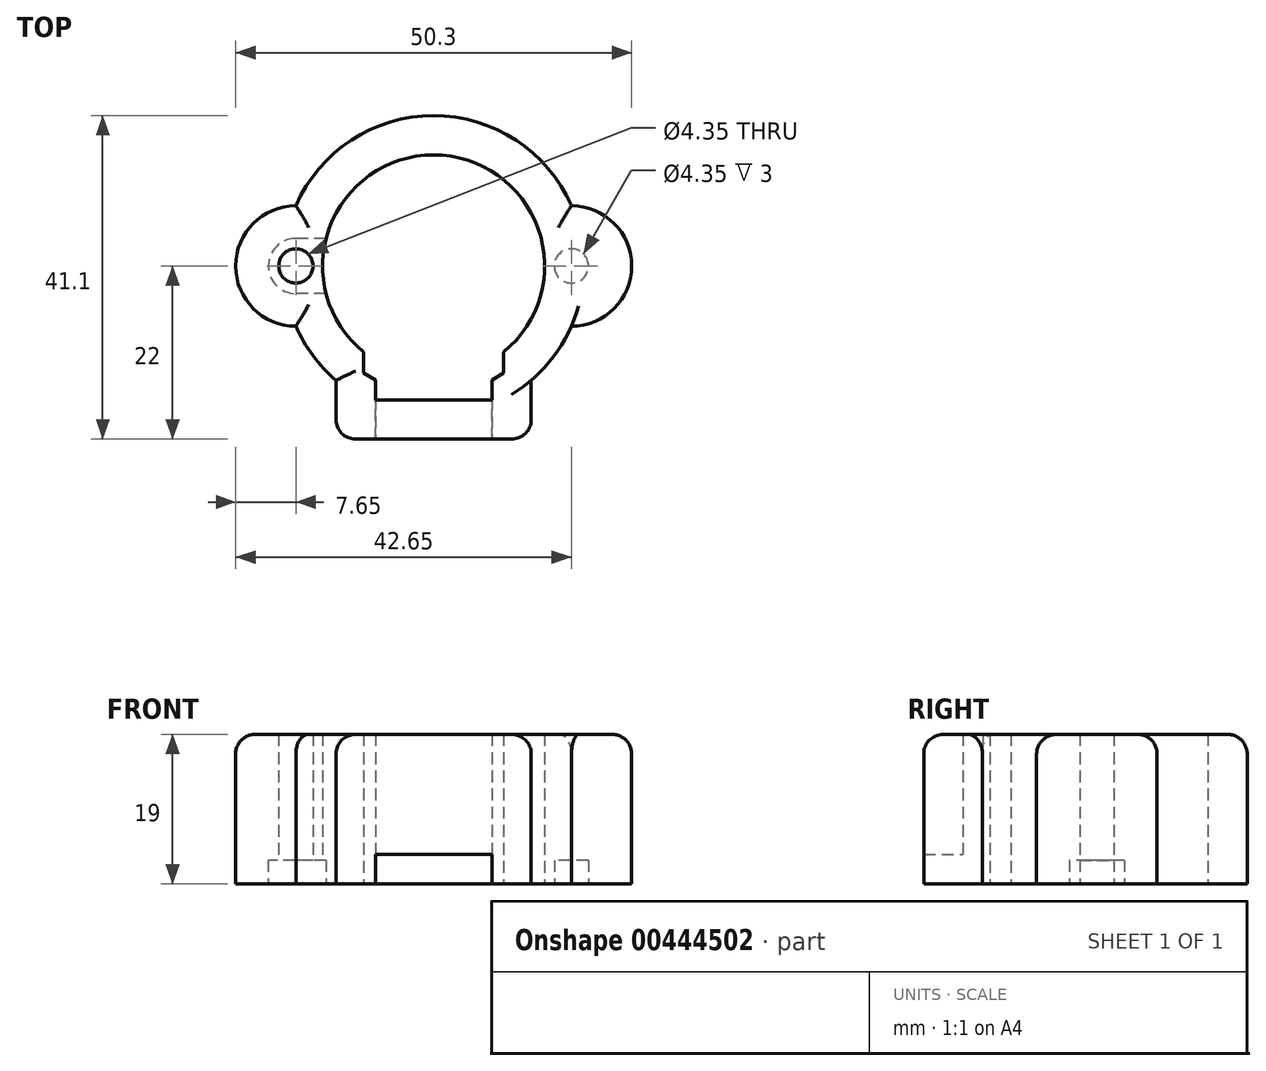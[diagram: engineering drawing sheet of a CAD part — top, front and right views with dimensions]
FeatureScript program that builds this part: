
annotation { "Feature Type Name" : "Feature", "Feature Type Description" : "" }
export const myFeature = defineFeature(function(context is Context, id is Id, definition is map)
    precondition{}
    {
        {
            var Q0;
            Q0=qCreatedBy(makeId("Top.planeOp"),FACE);
            var sketch = newSketch(context, id + "F0", { "sketchPlane" : qUnion([Q0])});
            skCircle(sketch, "E0", {"center": v(0, 0) * mm, "radius": 14.1 * mm});
            skLineSegment(sketch, "E1", {"start": v(-39.09, 0) * mm, "end": v(52.58, 0) * mm, "construction": true});
            skLineSegment(sketch, "E2", {"start": v(0, -22) * mm, "end": v(0, -37.4) * mm, "construction": true});
            skCircle(sketch, "E3", {"center": v(17.5, 0) * mm, "radius": 2.18 * mm});
            skLineSegment(sketch, "E4", {"start": v(0, 3.5) * mm, "end": v(17.5, 3.5) * mm});
            skArc(sketch, "E5", {"start": v(17.5, 3.5) * mm, "mid": v(19.97, 2.47) * mm, "end": v(21, 0) * mm});
            skLineSegment(sketch, "E6.MirrorCS", {"start": v(0, -3.5) * mm, "end": v(17.5, -3.5) * mm});
            skArc(sketch, "E7.MirrorCS", {"start": v(17.5, -3.5) * mm, "mid": v(19.97, -2.47) * mm, "end": v(21, 0) * mm});
            skLineSegment(sketch, "E8.MirrorCS", {"start": v(0, 3.5) * mm, "end": v(-17.5, 3.5) * mm});
            skLineSegment(sketch, "E9.MirrorCS", {"start": v(0, -3.5) * mm, "end": v(-17.5, -3.5) * mm});
            skArc(sketch, "E10.MirrorCS", {"start": v(-17.5, -3.5) * mm, "mid": v(-19.97, -2.47) * mm, "end": v(-21, 0) * mm});
            skArc(sketch, "E11.MirrorCS", {"start": v(-17.5, 3.5) * mm, "mid": v(-19.97, 2.47) * mm, "end": v(-21, 0) * mm});
            skCircle(sketch, "E12.MirrorC", {"center": v(-17.5, 0) * mm, "radius": 2.18 * mm});
            skLineSegment(sketch, "E13.bottom", {"start": v(0, 0) * mm, "end": v(7.4, 0) * mm});
            skLineSegment(sketch, "E13.top", {"start": v(0, -17) * mm, "end": v(7.4, -17) * mm});
            skLineSegment(sketch, "E13.left", {"start": v(0, 0) * mm, "end": v(0, -17) * mm});
            skLineSegment(sketch, "E13.right", {"start": v(7.4, 0) * mm, "end": v(7.4, -17) * mm});
            skPoint(sketch, "E14", {"position": v(7.4, -12) * mm});
            skPoint(sketch, "E15", {"position": v(7.4, -14.5) * mm});
            skLineSegment(sketch, "E16", {"start": v(7.4, -14.5) * mm, "end": v(8.9, -13.58) * mm});
            skLineSegment(sketch, "E17", {"start": v(8.9, -13.58) * mm, "end": v(8.9, -10.94) * mm});
            skLineSegment(sketch, "E18", {"start": v(7.4, -12) * mm, "end": v(21.19, -3.5) * mm, "construction": true});
            skLineSegment(sketch, "E19.MirrorCS", {"start": v(0, -17) * mm, "end": v(-7.4, -17) * mm});
            skLineSegment(sketch, "E20.MirrorCS", {"start": v(-7.4, 0) * mm, "end": v(-7.4, -17) * mm});
            skLineSegment(sketch, "E21.MirrorCS", {"start": v(-8.9, -13.58) * mm, "end": v(-8.9, -10.94) * mm});
            skLineSegment(sketch, "E22.MirrorCS", {"start": v(-7.4, -14.5) * mm, "end": v(-8.9, -13.58) * mm});
            skLineSegment(sketch, "E23.left", {"start": v(0, -3.5) * mm, "end": v(0, 3.5) * mm});
            skLineSegment(sketch, "E24.left", {"start": v(7.4, 0) * mm, "end": v(7.4, -3.5) * mm});
            skPoint(sketch, "E25", {"position": v(7.4, 0) * mm});
            skLineSegment(sketch, "E26.left", {"start": v(0, 24) * mm, "end": v(0, -17) * mm});
            skArc(sketch, "E27", {"start": v(-17.5, -7.65) * mm, "mid": v(-25.15, 0) * mm, "end": v(-17.5, 7.65) * mm});
            skArc(sketch, "E28", {"start": v(-17.5, 7.65) * mm, "mid": v(0, 19.1) * mm, "end": v(17.5, 7.65) * mm});
            skArc(sketch, "E29", {"start": v(17.5, 7.65) * mm, "mid": v(25.15, 0) * mm, "end": v(17.5, -7.65) * mm});
            skArc(sketch, "E30", {"start": v(-17.5, -7.65) * mm, "mid": v(-15.34, -11.38) * mm, "end": v(-12.4, -14.53) * mm});
            skLineSegment(sketch, "E31.bottom", {"start": v(-7.4, -14.53) * mm, "end": v(7.4, -14.53) * mm});
            skLineSegment(sketch, "E31.top", {"start": v(-12.4, -22) * mm, "end": v(12.4, -22) * mm});
            skLineSegment(sketch, "E31.left", {"start": v(-12.4, -14.53) * mm, "end": v(-12.4, -22) * mm});
            skLineSegment(sketch, "E31.right", {"start": v(12.4, -14.53) * mm, "end": v(12.4, -22) * mm});
            skArc(sketch, "E32.trimOffspring", {"start": v(12.4, -14.53) * mm, "mid": v(16.07, -10.32) * mm, "end": v(18.37, -5.24) * mm});
            skLineSegment(sketch, "E33.trimOffspring", {"start": v(0, 0) * mm, "end": v(0, -17) * mm, "construction": true});
            skLineSegment(sketch, "E34.trimOffspring", {"start": v(0, -22) * mm, "end": v(0, -24) * mm});
            skSolve(sketch);
        }
        {
            var Q0;
            {var subQ5=sQuery(id+"F0.wireOp",EDGE,"E5");Q0=makeQuery(id+"F0.imprint","IMPRINT",FACE,{"disambiguationData":[TD([[makeQuery(id+"F0.imprint","IMPRINT",EDGE,{"derivedFrom":subQ5}),1.0]])]});}
            var Q1;
            {var subQ0=sQuery(id+"F0.wireOp",EDGE,"E10.MirrorCS");Q1=makeQuery(id+"F0.imprint","IMPRINT",FACE,{"disambiguationData":[TD([[makeQuery(id+"F0.imprint","IMPRINT",EDGE,{"derivedFrom":subQ0}),-1.0]])]});}
            var Q2;
            Q2=makeQuery(id+"F0.imprint","IMPRINT",FACE,{"disambiguationData":[TD([[makeQuery(id+"F0.imprint","IMPRINT",EDGE,{"derivedFrom":sQuery(id+"F0.wireOp",EDGE,"E12.MirrorC")}),-1.0]])]});
            var Q3;
            Q3=makeQuery(id+"F0.imprint","IMPRINT",FACE,{"disambiguationData":[TD([[makeQuery(id+"F0.imprint","IMPRINT",EDGE,{"derivedFrom":sQuery(id+"F0.wireOp",EDGE,"E3")}),-1.0]])]});
            var Q4;
            Q4=makeQuery(id+"F0.imprint","IMPRINT",FACE,{"disambiguationData":[TD([[makeQuery(id+"F0.imprint","IMPRINT",EDGE,{"derivedFrom":sQuery(id+"F0.wireOp",EDGE,"E3")}),1.0]])]});
            var Q5;
            {var subQ6=sQuery(id+"F0.wireOp",EDGE,"E10.MirrorCS");Q5=makeQuery(id+"F0.imprint","IMPRINT",FACE,{"disambiguationData":[TD([[makeQuery(id+"F0.imprint","IMPRINT",EDGE,{"derivedFrom":subQ6}),1.0]])]});}
            var Q6;
            {var subQ5=sQuery(id+"F0.wireOp",EDGE,"E23.right");Q6=makeQuery(id+"F0.imprint","IMPRINT",FACE,{"disambiguationData":[TD([[makeQuery(id+"F0.imprint","IMPRINT",EDGE,{"derivedFrom":subQ5}),1.0]])]});}
            var Q7;
            {var subQ5=sQuery(id+"F0.wireOp",EDGE,"E24.right");Q7=makeQuery(id+"F0.imprint","IMPRINT",FACE,{"disambiguationData":[TD([[makeQuery(id+"F0.imprint","IMPRINT",EDGE,{"derivedFrom":subQ5}),-1.0]])]});}
            var Q8;
            {var subQ0=sQuery(id+"F0.wireOp",EDGE,"E26.top");Q8=makeQuery(id+"F0.imprint","IMPRINT",FACE,{"disambiguationData":[TD([[makeQuery(id+"F0.imprint","IMPRINT",EDGE,{"derivedFrom":subQ0}),-1.0]])]});}
            var Q9;
            {var subQ1=sQuery(id+"F0.wireOp",EDGE,"E13.top");Q9=makeQuery(id+"F0.imprint","IMPRINT",FACE,{"disambiguationData":[TD([[makeQuery(id+"F0.imprint","IMPRINT",EDGE,{"derivedFrom":subQ1}),-1.0]])]});}
            var Q10;
            {var subQ0=sQuery(id+"F0.wireOp",EDGE,"E24.bottom");var subQ1=sQuery(id+"F0.wireOp",EDGE,"E0");var subQ2=makeQuery(id+"F0.imprint","INTERSECT",VERTEX,{"derivedFrom":[subQ1,subQ0]});Q10=makeQuery(id+"F0.imprint","IMPRINT",FACE,{"disambiguationData":[TD([[makeQuery(id+"F0.imprint","IMPRINT",EDGE,{"disambiguationData":[TD([[subQ2,-1.0]])],"derivedFrom":subQ1}),-1.0]])]});}
            var Q11;
            {var subQ0=sQuery(id+"F0.wireOp",EDGE,"E26.bottom");Q11=makeQuery(id+"F0.imprint","IMPRINT",FACE,{"disambiguationData":[TD([[makeQuery(id+"F0.imprint","IMPRINT",EDGE,{"derivedFrom":subQ0}),1.0]])]});}
            extrude(context, id + "F1", {"entities" : qUnion([Q0, Q1, Q2, Q3, Q4, Q5, Q6, Q7, Q8, Q9, Q10, Q11]), "depth" : 21 * mm});
        }
        {
            var Q0;
            Q0=makeQuery(id+"F0.imprint","IMPRINT",FACE,{"disambiguationData":[TD([[makeQuery(id+"F0.imprint","IMPRINT",EDGE,{"derivedFrom":sQuery(id+"F0.wireOp",EDGE,"E3")}),-1.0]])]});
            var Q1;
            {var subQ0=sQuery(id+"F0.wireOp",EDGE,"E10.MirrorCS");Q1=makeQuery(id+"F0.imprint","IMPRINT",FACE,{"disambiguationData":[TD([[makeQuery(id+"F0.imprint","IMPRINT",EDGE,{"derivedFrom":subQ0}),-1.0]])]});}
            extrude(context, id + "F2", {"entities" : qUnion([Q0, Q1]), "operationType" : NewBodyOperationType.REMOVE, "depth" : 2 * mm});
        }
        {
            var Q0;
            Q0=makeQuery(id+"F0.imprint","IMPRINT",FACE,{"disambiguationData":[TD([[makeQuery(id+"F0.imprint","IMPRINT",EDGE,{"derivedFrom":sQuery(id+"F0.wireOp",EDGE,"E3")}),1.0]])]});
            var Q1;
            Q1=makeQuery(id+"F0.imprint","IMPRINT",FACE,{"disambiguationData":[TD([[makeQuery(id+"F0.imprint","IMPRINT",EDGE,{"derivedFrom":sQuery(id+"F0.wireOp",EDGE,"E12.MirrorC")}),-1.0]])]});
            extrude(context, id + "F3", {"entities" : qUnion([Q0, Q1]), "operationType" : NewBodyOperationType.REMOVE, "depth" : 5 * mm});
        }
        {
            var Q0;
            Q0=makeQuery(id+"F1.opExtrude","SWEPT_FACE",FACE,{"disambiguationData":[OSD([sQuery(id+"F0.wireOp",EDGE,"E13.top"),sQuery(id+"F0.wireOp",EDGE,"E19.MirrorCS")])]});
            var sketch = newSketch(context, id + "F4", { "sketchPlane" : qUnion([Q0])});
            skLineSegment(sketch, "E35.bottom", {"start": v(-7.4, 0) * mm, "end": v(7.4, 0) * mm});
            skLineSegment(sketch, "E35.top", {"start": v(-7.4, 5.75) * mm, "end": v(7.4, 5.75) * mm});
            skLineSegment(sketch, "E35.left", {"start": v(-7.4, 0) * mm, "end": v(-7.4, 5.75) * mm});
            skLineSegment(sketch, "E35.right", {"start": v(7.4, 0) * mm, "end": v(7.4, 5.75) * mm});
            skSolve(sketch);
        }
        {
            var Q0;
            Q0=qSketchRegion(id+"F4",true);
            extrude(context, id + "F5", {"entities" : qUnion([Q0]), "operationType" : NewBodyOperationType.REMOVE, "endBound" : BoundingType.UP_TO_NEXT, "oppositeDirection" : true, "depth" : 25 * mm});
        }
        {
            var Q0;
            Q0=makeQuery(id+"F1.opExtrude","CAP_EDGE",EDGE,{"disambiguationData":[OSD([sQuery(id+"F0.wireOp",EDGE,"E28")])],"isStart":true});
            var Q1;
            Q1=makeQuery(id+"F1.opExtrude","CAP_EDGE",EDGE,{"disambiguationData":[OSD([sQuery(id+"F0.wireOp",EDGE,"E27")])],"isStart":true});
            var Q2;
            Q2=makeQuery(id+"F1.opExtrude","CAP_EDGE",EDGE,{"disambiguationData":[OSD([sQuery(id+"F0.wireOp",EDGE,"E30")])],"isStart":true});
            var Q3;
            Q3=makeQuery(id+"F1.opExtrude","CAP_EDGE",EDGE,{"disambiguationData":[OSD([sQuery(id+"F0.wireOp",EDGE,"E31.left")])],"isStart":true});
            var Q4;
            Q4=makeQuery(id+"F1.opExtrude","CAP_EDGE",EDGE,{"disambiguationData":[OSD([sQuery(id+"F0.wireOp",EDGE,"E31.right")])],"isStart":true});
            var Q5;
            Q5=makeQuery(id+"F1.opExtrude","CAP_EDGE",EDGE,{"disambiguationData":[OSD([sQuery(id+"F0.wireOp",EDGE,"E32.trimOffspring")])],"isStart":true});
            var Q6;
            Q6=makeQuery(id+"F1.opExtrude","CAP_EDGE",EDGE,{"disambiguationData":[OSD([sQuery(id+"F0.wireOp",EDGE,"E29")])],"isStart":true});
            var Q7;
            Q7=makeQuery(id+"F1.opExtrude","CAP_EDGE",EDGE,{"disambiguationData":[OSD([sQuery(id+"F0.wireOp",EDGE,"E28")])],"isStart":false});
            var Q8;
            Q8=makeQuery(id+"F1.opExtrude","CAP_EDGE",EDGE,{"disambiguationData":[OSD([sQuery(id+"F0.wireOp",EDGE,"E29")])],"isStart":false});
            var Q9;
            Q9=makeQuery(id+"F1.opExtrude","CAP_EDGE",EDGE,{"disambiguationData":[OSD([sQuery(id+"F0.wireOp",EDGE,"E27")])],"isStart":false});
            var Q10;
            Q10=makeQuery(id+"F1.opExtrude","CAP_EDGE",EDGE,{"disambiguationData":[OSD([sQuery(id+"F0.wireOp",EDGE,"E30")])],"isStart":false});
            var Q11;
            Q11=makeQuery(id+"F1.opExtrude","CAP_EDGE",EDGE,{"disambiguationData":[OSD([sQuery(id+"F0.wireOp",EDGE,"E31.left")])],"isStart":false});
            var Q12;
            Q12=makeQuery(id+"F1.opExtrude","CAP_EDGE",EDGE,{"disambiguationData":[OSD([sQuery(id+"F0.wireOp",EDGE,"E31.right")])],"isStart":false});
            var Q13;
            Q13=makeQuery(id+"F1.opExtrude","CAP_EDGE",EDGE,{"disambiguationData":[OSD([sQuery(id+"F0.wireOp",EDGE,"E31.top")])],"isStart":false});
            var Q14;
            Q14=makeQuery(id+"F1.opExtrude","SWEPT_EDGE",EDGE,{"disambiguationData":[OSD([sQuery(id+"F0.wireOp",EDGE,"E31.top"),sQuery(id+"F0.wireOp",EDGE,"E31.left")])]});
            var Q15;
            Q15=makeQuery(id+"F1.opExtrude","SWEPT_EDGE",EDGE,{"disambiguationData":[OSD([sQuery(id+"F0.wireOp",EDGE,"E31.top"),sQuery(id+"F0.wireOp",EDGE,"E31.right")])]});
            var Q16;
            {var subQ1=sQuery(id+"F0.wireOp",EDGE,"E31.top");var subQ2=sQuery(id+"F0.wireOp",EDGE,"E20.MirrorCS");Q16=makeQuery(id+"F5.boolean.opBoolean","SPLIT",EDGE,{"disambiguationData":[TD([makeQuery(id+"F1.opExtrude","SWEPT_FACE",FACE,{"disambiguationData":[OSD([subQ2])]})])],"derivedFrom":makeQuery(id+"F1.opExtrude","CAP_EDGE",EDGE,{"disambiguationData":[OSD([subQ1])],"isStart":true})});}
            var Q17;
            {var subQ0=sQuery(id+"F0.wireOp",EDGE,"E31.top");var subQ1=sQuery(id+"F0.wireOp",EDGE,"E13.right");Q17=makeQuery(id+"F5.boolean.opBoolean","SPLIT",EDGE,{"disambiguationData":[TD([makeQuery(id+"F1.opExtrude","SWEPT_FACE",FACE,{"disambiguationData":[OSD([subQ1])]})])],"derivedFrom":makeQuery(id+"F1.opExtrude","CAP_EDGE",EDGE,{"disambiguationData":[OSD([subQ0])],"isStart":true})});}
            fillet(context, id + "F6", {"entities" : qUnion([Q0, Q1, Q2, Q3, Q4, Q5, Q6, Q7, Q8, Q9, Q10, Q11, Q12, Q13, Q14, Q15, Q16, Q17]), "radius" : 2.5 * mm, "tangentPropagation" : true, "allowEdgeOverflow" : false});
        }
    });
